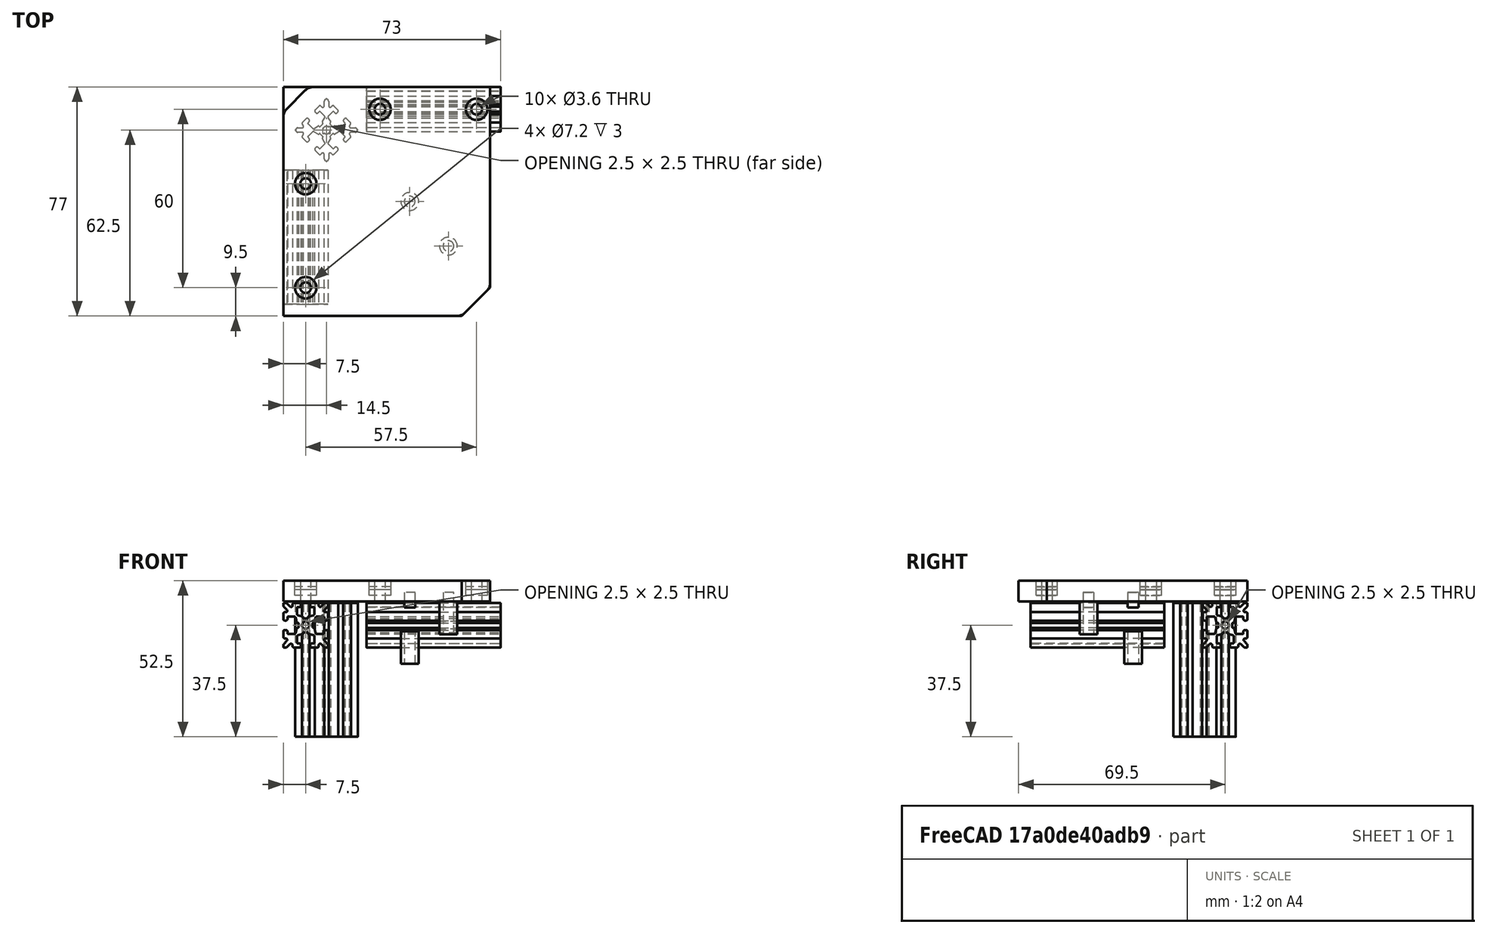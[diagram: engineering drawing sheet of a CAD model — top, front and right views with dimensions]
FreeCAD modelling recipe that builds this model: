
FCSTD DOCUMENT  (FreeCAD 0.15R4671 (Git))
Label: TopCornerCapIdler_II
License: All rights reserved
LicenseURL: http://en.wikipedia.org/wiki/All_rights_reserved
objects: Part::Feature×5, Mesh::Feature×5, Sketcher::SketchObject×4, PartDesign::Pocket×3, PartDesign::Fillet×2, PartDesign::Pad×1
note: 19 computed .brp shape members not serialized (recipe doc carries the construction recipe); baked Part::Feature solids carry a one-line shape summary decoded from their .brp

FEATURE [Sketcher::SketchObject] Sketch
  Placement = pos=(0,0,2) rot=(0,0,1;0rad)
  sketch-geometry (9):
    g0: LineSegment StartX=-7.5 StartY=7.5 StartZ=0 EndX=62.0538 EndY=7.5 EndZ=0
    g1: LineSegment StartX=62.0538 StartY=7.5 StartZ=0 EndX=62.0538 EndY=-59.9462 EndZ=0
    g2: LineSegment StartX=62.0538 StartY=-59.9462 StartZ=0 EndX=52.5 EndY=-69.5 EndZ=0
    g3: LineSegment StartX=52.5 StartY=-69.5 StartZ=0 EndX=-7.5 EndY=-69.5 EndZ=0
    g4: LineSegment StartX=-7.5 StartY=-69.5 StartZ=0 EndX=-7.5 EndY=7.5 EndZ=0
    g5: Circle CenterX=25 CenterY=0 CenterZ=0 NormalX=0 NormalY=0 NormalZ=1 Radius=1.8
    g6: Circle CenterX=57.5 CenterY=0 CenterZ=0 NormalX=0 NormalY=0 NormalZ=1 Radius=1.8
    g7: Circle CenterX=0 CenterY=-25 CenterZ=0 NormalX=0 NormalY=0 NormalZ=1 Radius=1.8
    g8: Circle CenterX=0 CenterY=-60 CenterZ=0 NormalX=0 NormalY=0 NormalZ=1 Radius=1.8
  constraints (16):
    c: Coincident(g0,g1)
    c: Coincident(g1,g2)
    c: Coincident(g2,g3)
    c: Coincident(g3,g4)
    c: Coincident(g4,g0)
    c: Horizontal(g3)
    c: Horizontal(g0)
    c: Vertical(g1)
    c: Vertical(g4)
    c: Angle(g2,g-2) = 0.785398
    c: DistanceX(g0) = -7.5
    c: DistanceY(g0) = 7.5
    c: Radius(g5) = 1.8
    c: Radius(g6) = 1.8
    c: Radius(g7) = 1.8
    c: Radius(g8) = 1.8
FEATURE [Part::Feature] Part__Feature  label="OB1515_45mm001"
  Placement = pos=(0,-20.5,-6) rot=(1,0,0;1.5708rad)
  shape: bbox 15 x 45 x 15 mm, 158 faces (baked)
FEATURE [Part::Feature] Part__Feature001  label="OB1515_45mm002"
  Placement = pos=(20.5,0,-6) rot=(0.57735,0.57735,0.57735;2.0944rad)
  shape: bbox 45 x 15 x 15 mm, 158 faces (baked)
FEATURE [Part::Feature] Part__Feature002  label="OB1515_45mm"
  Placement = pos=(7,-7,-43.5) rot=(0,0,1;0.785398rad)
  shape: bbox 21.01 x 21.01 x 45 mm, 158 faces (baked)
FEATURE [PartDesign::Pad] Pad
  Length = 7
  Length2 = 100
  Placement = pos=(0,0,2) rot=(0,0,1;0rad)
  Sketch = -> Sketch
  Type = 0
FEATURE [Sketcher::SketchObject] Sketch001
  Placement = pos=(0,0,9) rot=(0,0,1;0rad)
  Support = -> Pad [Face11]
  sketch-geometry (4):
    g0: Circle CenterX=57.5 CenterY=0 CenterZ=0 NormalX=0 NormalY=0 NormalZ=1 Radius=3.6
    g1: Circle CenterX=25 CenterY=0 CenterZ=0 NormalX=0 NormalY=0 NormalZ=1 Radius=3.6
    g2: Circle CenterX=0 CenterY=-25 CenterZ=0 NormalX=0 NormalY=0 NormalZ=1 Radius=3.6
    g3: Circle CenterX=0 CenterY=-60 CenterZ=0 NormalX=0 NormalY=0 NormalZ=1 Radius=3.6
  constraints (4):
    c: Radius(g0) = 3.6
    c: Radius(g1) = 3.6
    c: Radius(g2) = 3.6
    c: Radius(g3) = 3.6
FEATURE [PartDesign::Pocket] Pocket
  Length = 3
  Placement = pos=(0,0,2) rot=(0,0,1;0rad)
  Sketch = -> Sketch001
  Type = 0
FEATURE [Mesh::Feature] temp
FEATURE [Sketcher::SketchObject] Sketch002
  Placement = pos=(0,0,9) rot=(0,0,1;0rad)
  Support = -> Pocket [Face5]
  sketch-geometry (5):
    g0: LineSegment StartX=-8.5 StartY=-1 StartZ=0 EndX=-7.5 EndY=-1 EndZ=0
    g1: LineSegment StartX=-7.5 StartY=-1 StartZ=0 EndX=1 EndY=7.5 EndZ=0
    g2: LineSegment StartX=1 StartY=7.5 StartZ=0 EndX=1 EndY=8.5 EndZ=0
    g3: LineSegment StartX=1 StartY=8.5 StartZ=0 EndX=-8.5 EndY=8.5 EndZ=0
    g4: LineSegment StartX=-8.5 StartY=8.5 StartZ=0 EndX=-8.5 EndY=-1 EndZ=0
  constraints (5):
    c: Coincident(g0,g1)
    c: Coincident(g1,g2)
    c: Coincident(g2,g3)
    c: Coincident(g3,g4)
    c: Coincident(g4,g0)
FEATURE [PartDesign::Pocket] Pocket001
  Length = 5
  Placement = pos=(0,0,2) rot=(0,0,1;0rad)
  Sketch = -> Sketch002
  Type = 1
FEATURE [PartDesign::Fillet] Fillet
  Base = -> Pocket001 [Edge4,Edge24]
  Placement = pos=(0,0,2) rot=(0,0,1;0rad)
  Radius = 4
FEATURE [PartDesign::Fillet] Fillet001
  Base = -> Fillet [Edge30,Edge18]
  Placement = pos=(0,0,2) rot=(0,0,1;0rad)
  Radius = 4
FEATURE [Mesh::Feature] _x10x4_FlangedBearing  label="5x10x4_FlangedBearing_T001"
  Placement = pos=(35,-31,-1) rot=(-1,0,0;1.5708rad)
FEATURE [Mesh::Feature] _x10x4_FlangedBearing001  label="5x10x4_FlangedBearing_B001"
  Placement = pos=(35,-31,-5) rot=(1,0,0;1.5708rad)
FEATURE [Mesh::Feature] _x10x4_FlangedBearing002  label="5x10x4_FlangedBearing_T"
  Placement = pos=(48,-46,-12) rot=(-1,0,0;1.5708rad)
FEATURE [Mesh::Feature] _x10x4_FlangedBearing003  label="5x10x4_FlangedBearing_B"
  Placement = pos=(48,-46,-16) rot=(1,0,0;1.5708rad)
FEATURE [Part::Feature] Part__Feature003  label="IdlerBearingStandoff"
  Placement = pos=(48,-46,-9) rot=(0,0,1;0rad)
  shape: bbox 6 x 6 x 11 mm, 4 faces (baked)
FEATURE [Part::Feature] Part__Feature004  label="IdlerBearingStandoff001"
  Placement = pos=(35,-31,-19) rot=(0,0,1;0rad)
  shape: bbox 6 x 6 x 11 mm, 4 faces (baked)
FEATURE [Sketcher::SketchObject] Sketch003
  Placement = pos=(0,0,2) rot=(1,0,0;3.14159rad)
  Support = -> Fillet001 [Face1]
  sketch-geometry (2):
    g0: Circle CenterX=35 CenterY=31 CenterZ=0 NormalX=0 NormalY=0 NormalZ=1 Radius=1.8
    g1: Circle CenterX=48 CenterY=46 CenterZ=0 NormalX=0 NormalY=0 NormalZ=1 Radius=1.8
  constraints (2):
    c: Radius(g1) = 1.8
    c: Equal(g1,g0)
FEATURE [PartDesign::Pocket] Pocket002  label="TopCornerCapIdler_II"
  Length = 5
  Placement = pos=(0,0,2) rot=(0,0,1;0rad)
  Sketch = -> Sketch003
  Type = 0
